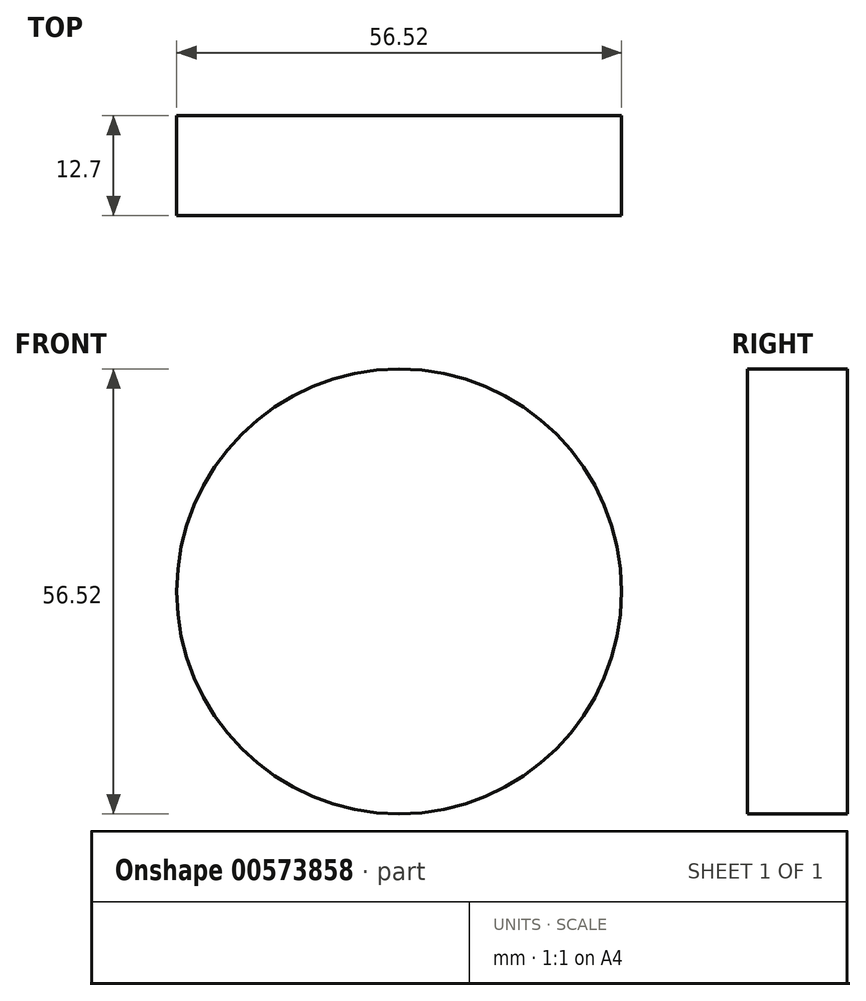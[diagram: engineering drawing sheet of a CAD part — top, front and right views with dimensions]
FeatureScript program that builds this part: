
annotation { "Feature Type Name" : "Feature", "Feature Type Description" : "" }
export const myFeature = defineFeature(function(context is Context, id is Id, definition is map)
    precondition{}
    {
        {
            var Q0;
            Q0=qCreatedBy(makeId("Front.planeOp"),FACE);
            var sketch = newSketch(context, id + "F0", { "sketchPlane" : qUnion([Q0])});
            skCircle(sketch, "E0", {"center": v(0, 0) * mm, "radius": 28.26 * mm});
            skSolve(sketch);
        }
        {
            var Q0;
            Q0=makeQuery(id+"F0.imprint","IMPRINT",FACE,{"disambiguationData":[TD([[makeQuery(id+"F0.imprint","IMPRINT",EDGE,{"derivedFrom":sQuery(id+"F0.wireOp",EDGE,"E0")}),1.0]])]});
            extrude(context, id + "F1", {"entities" : qUnion([Q0]), "depth" : 12.7 * mm, "offsetDistance" : 25.4 * mm});
        }
    });
